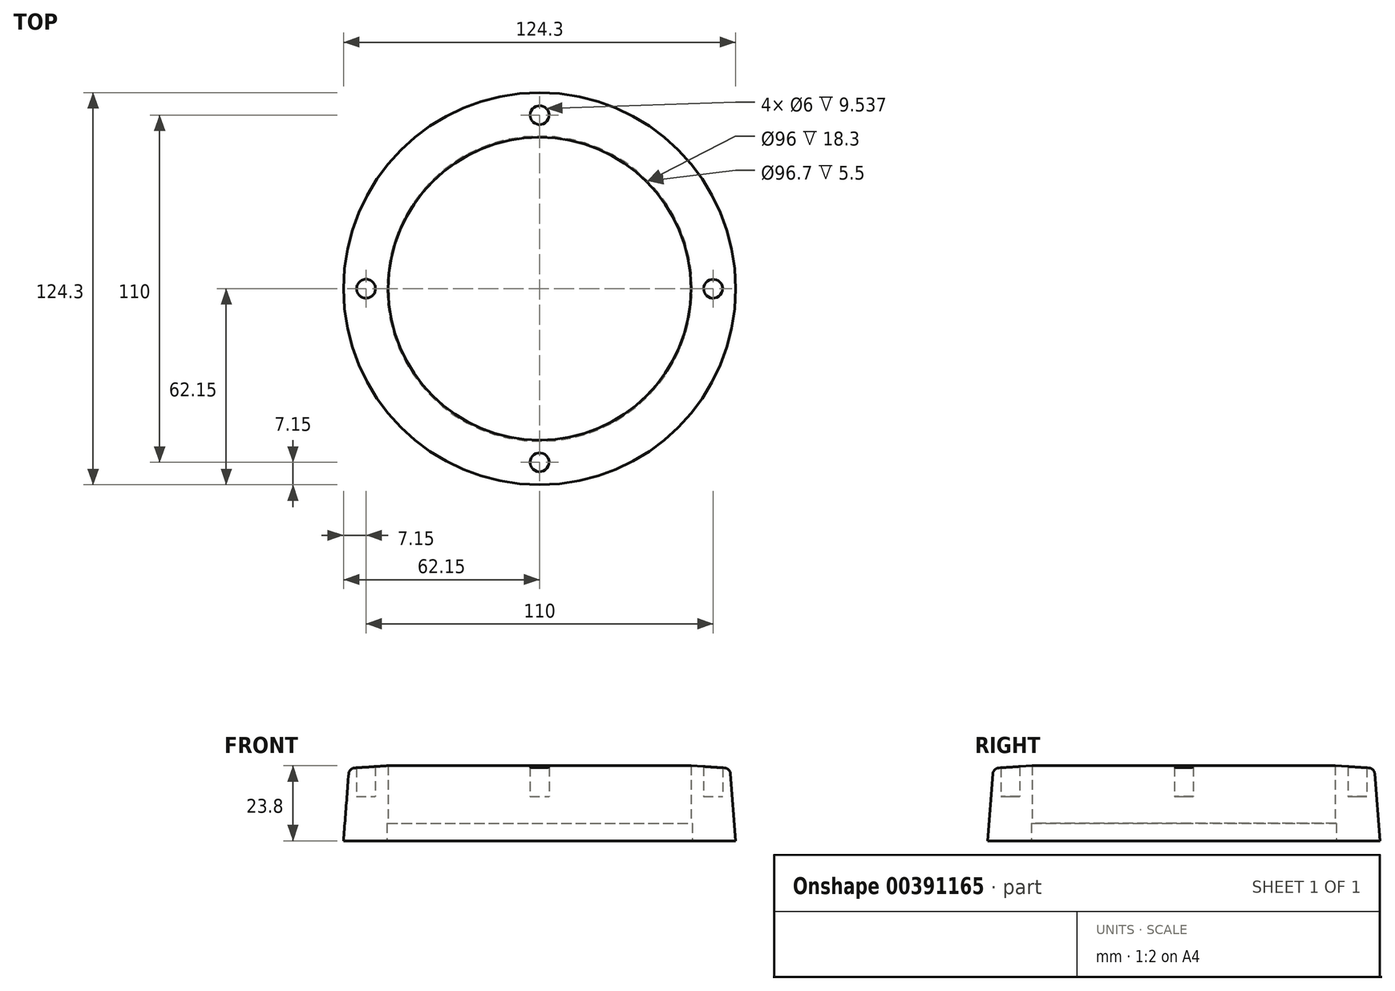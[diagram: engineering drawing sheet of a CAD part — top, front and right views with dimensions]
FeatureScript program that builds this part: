
annotation { "Feature Type Name" : "Feature", "Feature Type Description" : "" }
export const myFeature = defineFeature(function(context is Context, id is Id, definition is map)
    precondition{}
    {
        {
            var Q0;
            Q0=qCreatedBy(makeId("Front.planeOp"),FACE);
            var sketch = newSketch(context, id + "F0", { "sketchPlane" : qUnion([Q0])});
            skLineSegment(sketch, "E0", {"start": v(0, -58.94) * mm, "end": v(0, 82.9) * mm, "construction": true});
            skLineSegment(sketch, "E1", {"start": v(62.15, 0) * mm, "end": v(60.5, 21.26) * mm});
            skArc(sketch, "E2", {"start": v(60.5, 21.26) * mm, "mid": v(59.91, 22.53) * mm, "end": v(58.64, 23.1) * mm});
            skLineSegment(sketch, "E3", {"start": v(48, 5.5) * mm, "end": v(48, 23.8) * mm});
            skLineSegment(sketch, "E4", {"start": v(48, 23.8) * mm, "end": v(58.64, 23.1) * mm});
            skText(sketch, "E5", { "text": "5 navoja\ntrapezni navoj, precnik 95 mm, korak 4 mm\nu dnu trapezni, ali na vrhu zubaca R=1\ntako da je na vrhu potpuno zaobljen", "fontName": "OpenSans-Regular.ttf"});
            skLineSegment(sketch, "E6", {"start": v(33.72, 35.3) * mm, "end": v(48, 14.65) * mm, "construction": true});
            skLineSegment(sketch, "E7", {"start": v(48, 5.5) * mm, "end": v(48.35, 5.5) * mm});
            skLineSegment(sketch, "E8", {"start": v(48.35, 5.5) * mm, "end": v(48.35, 0) * mm});
            skLineSegment(sketch, "E9", {"start": v(62.15, 0) * mm, "end": v(48.35, 0) * mm});
            const initialGuessF0  = {"E5": [0.01254, 0.04714, 1, 0, 0.00179]};
            skSetInitialGuess(sketch, initialGuessF0);
            skSolve(sketch);
        }
        {
            var Q0;
            Q0=makeQuery(id+"F0.imprint","IMPRINT",FACE,{"disambiguationData":[TD([[makeQuery(id+"F0.imprint","IMPRINT",EDGE,{"derivedFrom":sQuery(id+"F0.wireOp",EDGE,"E1")}),1.0]])]});
            var Q1;
            Q1=sQuery(id+"F0.wireOp",EDGE,"E0");
            revolve(context, id + "F1", {"entities" : qUnion([Q0]), "axis" : qUnion([Q1]), "revolveType" : RevolveType.FULL});
        }
        {
            var Q0;
            Q0=makeQuery(id+"F1.opRevolve","SWEPT_FACE",FACE,{"disambiguationData":[OSD([sQuery(id+"F0.wireOp",EDGE,"E9")])]});
            var sketch = newSketch(context, id + "F2", { "sketchPlane" : qUnion([Q0])});
            skLineSegment(sketch, "E10", {"start": v(0, 67.26) * mm, "end": v(0, -67.5) * mm, "construction": true});
            skLineSegment(sketch, "E11", {"start": v(-70.32, 0) * mm, "end": v(69.3, 0) * mm, "construction": true});
            skCircle(sketch, "E12", {"center": v(0, 55) * mm, "radius": 3 * mm});
            skCircle(sketch, "E13", {"center": v(55, 0) * mm, "radius": 3 * mm});
            skCircle(sketch, "E14", {"center": v(0, -55) * mm, "radius": 3 * mm});
            skCircle(sketch, "E15", {"center": v(-55, 0) * mm, "radius": 3 * mm});
            skSolve(sketch);
        }
        {
            var Q0;
            Q0=makeQuery(id+"F2.imprint","IMPRINT",FACE,{"disambiguationData":[TD([[makeQuery(id+"F2.imprint","IMPRINT",EDGE,{"derivedFrom":sQuery(id+"F2.wireOp",EDGE,"E15")}),1.0]])]});
            var Q1;
            Q1=makeQuery(id+"F2.imprint","IMPRINT",FACE,{"disambiguationData":[TD([[makeQuery(id+"F2.imprint","IMPRINT",EDGE,{"derivedFrom":sQuery(id+"F2.wireOp",EDGE,"E12")}),1.0]])]});
            var Q2;
            Q2=makeQuery(id+"F2.imprint","IMPRINT",FACE,{"disambiguationData":[TD([[makeQuery(id+"F2.imprint","IMPRINT",EDGE,{"derivedFrom":sQuery(id+"F2.wireOp",EDGE,"E13")}),1.0]])]});
            var Q3;
            Q3=makeQuery(id+"F2.imprint","IMPRINT",FACE,{"disambiguationData":[TD([[makeQuery(id+"F2.imprint","IMPRINT",EDGE,{"derivedFrom":sQuery(id+"F2.wireOp",EDGE,"E14")}),1.0]])]});
            extrude(context, id + "F3", {"entities" : qUnion([Q0, Q1, Q2, Q3]), "operationType" : NewBodyOperationType.REMOVE, "oppositeDirection" : true, "depth" : 24 * mm, "hasSecondDirection" : true, "secondDirectionOppositeDirection" : true, "secondDirectionDepth" : 14 * mm});
        }
    });
